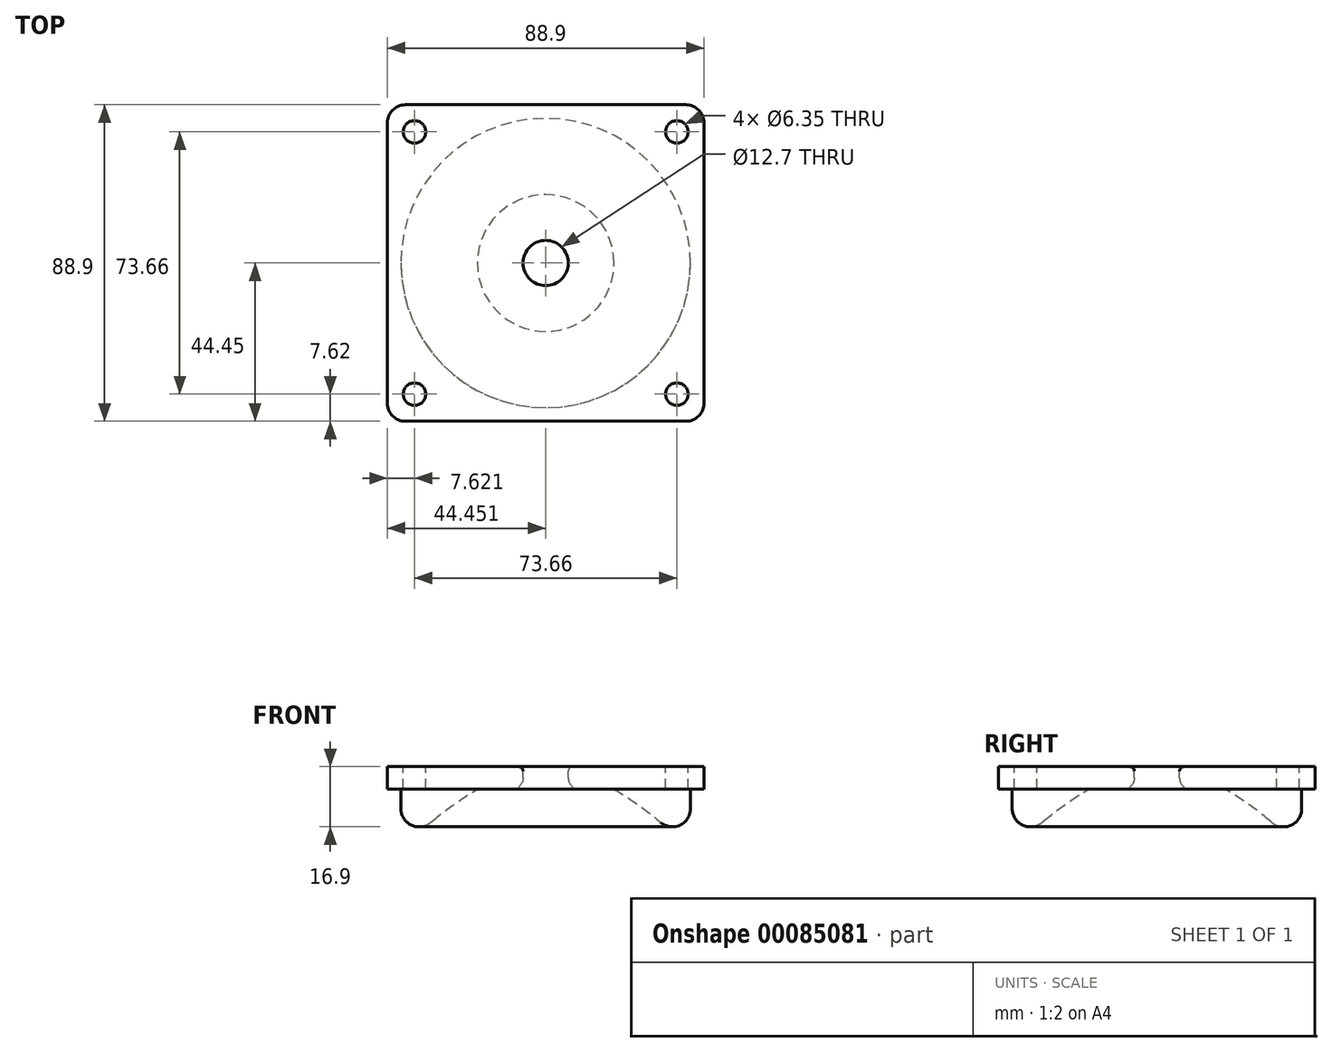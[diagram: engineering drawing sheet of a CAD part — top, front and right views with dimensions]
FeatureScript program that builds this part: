
annotation { "Feature Type Name" : "Feature", "Feature Type Description" : "" }
export const myFeature = defineFeature(function(context is Context, id is Id, definition is map)
    precondition{}
    {
        {
            var Q0;
            Q0=qCreatedBy(makeId("Front.planeOp"),FACE);
            var sketch = newSketch(context, id + "F0", { "sketchPlane" : qUnion([Q0])});
            skLineSegment(sketch, "E0", {"start": v(4.17, 45.04) * mm, "end": v(4.17, -20.37) * mm});
            skLineSegment(sketch, "E1", {"start": v(10.52, 12.1) * mm, "end": v(10.52, 30.43) * mm});
            skLineSegment(sketch, "E2.bottom", {"start": v(10.52, 30.43) * mm, "end": v(61.32, 30.43) * mm});
            skLineSegment(sketch, "E2.top", {"start": v(10.52, 24.08) * mm, "end": v(61.32, 24.08) * mm});
            skLineSegment(sketch, "E2.left", {"start": v(10.52, 30.43) * mm, "end": v(10.52, 24.08) * mm});
            skLineSegment(sketch, "E2.right", {"start": v(61.32, 30.43) * mm, "end": v(61.32, 24.08) * mm});
            skLineSegment(sketch, "E3", {"start": v(35.92, 15.19) * mm, "end": v(35.92, 24.08) * mm});
            skCircle(sketch, "E4", {"center": v(4.17, -20.37) * mm, "radius": 31.75 * mm});
            skFitSpline(sketch, "E5", {"points": [v(10.52, 30.43) * mm, v(35.92, 15.19) * mm, v(55.36, -11.12) * mm, v(53.77, -25.69) * mm, v(41.93, -25.69) * mm, v(36.47, -11.57) * mm, v(24.29, 4.78) * mm, v(10.52, 12.1) * mm], "startDerivative": vector(142.65, -59.66) * mm, "endDerivative": vector(-100.84, 59.34) * mm});
            skLineSegment(sketch, "E6", {"start": v(44.81, 24.08) * mm, "end": v(44.81, 6.32) * mm});
            skSolve(sketch);
        }
        {
            var Q0;
            {var subQ5=sQuery(id+"F0.wireOp",EDGE,"E2.bottom");Q0=makeQuery(id+"F0.imprint","IMPRINT",FACE,{"disambiguationData":[TD([[makeQuery(id+"F0.imprint","IMPRINT",EDGE,{"derivedFrom":subQ5}),-1.0]])]});}
            var Q1;
            {var subQ0=sQuery(id+"F0.wireOp",EDGE,"E2.left");Q1=makeQuery(id+"F0.imprint","IMPRINT",FACE,{"disambiguationData":[TD([[makeQuery(id+"F0.imprint","IMPRINT",EDGE,{"derivedFrom":subQ0}),1.0]])]});}
            var Q2;
            {var subQ0=sQuery(id+"F0.wireOp",EDGE,"E3");Q2=makeQuery(id+"F0.imprint","IMPRINT",FACE,{"disambiguationData":[TD([[makeQuery(id+"F0.imprint","IMPRINT",EDGE,{"derivedFrom":subQ0}),1.0]])]});}
            var Q3;
            {var subQ0=sQuery(id+"F0.wireOp",EDGE,"E1");Q3=makeQuery(id+"F0.imprint","IMPRINT",FACE,{"disambiguationData":[TD([[makeQuery(id+"F0.imprint","IMPRINT",EDGE,{"derivedFrom":subQ0}),-1.0]])]});}
            var Q4;
            {var subQ0=sQuery(id+"F0.wireOp",EDGE,"E3");Q4=makeQuery(id+"F0.imprint","IMPRINT",FACE,{"disambiguationData":[TD([[makeQuery(id+"F0.imprint","IMPRINT",EDGE,{"derivedFrom":subQ0}),-1.0]])]});}
            var Q5;
            Q5=sQuery(id+"F0.wireOp",EDGE,"E0");
            revolve(context, id + "F1", {"entities" : qUnion([Q0, Q1, Q2, Q3, Q4]), "axis" : qUnion([Q5]), "revolveType" : RevolveType.FULL});
        }
        {
            var Q0;
            Q0=makeQuery(id+"F1.opRevolve","SWEPT_EDGE",EDGE,{"disambiguationData":[OSD([sQuery(id+"F0.wireOp",EDGE,"E5"),sQuery(id+"F0.wireOp",EDGE,"E6")])]});
            fillet(context, id + "F2", {"entities" : qUnion([Q0]), "radius" : 5.08 * mm, "tangentPropagation" : true, "allowEdgeOverflow" : false});
        }
        {
            var Q0;
            Q0=makeQuery(id+"F1.opRevolve","SWEPT_FACE",FACE,{"disambiguationData":[OSD([sQuery(id+"F0.wireOp",EDGE,"E2.bottom")])]});
            var sketch = newSketch(context, id + "F3", { "sketchPlane" : qUnion([Q0])});
            skLineSegment(sketch, "E7.bottom", {"start": v(-52.98, 57.15) * mm, "end": v(61.32, 57.15) * mm});
            skLineSegment(sketch, "E7.top", {"start": v(-52.98, -57.15) * mm, "end": v(61.32, -57.15) * mm});
            skLineSegment(sketch, "E7.left", {"start": v(-52.98, 57.15) * mm, "end": v(-52.98, -57.15) * mm});
            skLineSegment(sketch, "E7.right", {"start": v(61.32, 57.15) * mm, "end": v(61.32, -57.15) * mm});
            skCircle(sketch, "E8", {"center": v(-32.66, 36.83) * mm, "radius": 3.18 * mm});
            skCircle(sketch, "E9", {"center": v(41, 36.83) * mm, "radius": 3.18 * mm});
            skCircle(sketch, "E10", {"center": v(41, -36.83) * mm, "radius": 3.18 * mm});
            skCircle(sketch, "E11", {"center": v(-32.66, -36.83) * mm, "radius": 3.18 * mm});
            skLineSegment(sketch, "E12.bottom", {"start": v(-40.28, 44.45) * mm, "end": v(48.62, 44.45) * mm});
            skLineSegment(sketch, "E12.top", {"start": v(-40.28, -44.45) * mm, "end": v(48.62, -44.45) * mm});
            skLineSegment(sketch, "E12.left", {"start": v(-40.28, 44.45) * mm, "end": v(-40.28, -44.45) * mm});
            skLineSegment(sketch, "E12.right", {"start": v(48.62, 44.45) * mm, "end": v(48.62, -44.45) * mm});
            skSolve(sketch);
        }
        {
            var Q0;
            Q0=makeQuery(id+"F3.imprint","IMPRINT",FACE,{"disambiguationData":[TD([[makeQuery(id+"F3.imprint","IMPRINT",EDGE,{"derivedFrom":sQuery(id+"F3.wireOp",EDGE,"E9")}),1.0]])]});
            var Q1;
            Q1=makeQuery(id+"F3.imprint","IMPRINT",FACE,{"disambiguationData":[TD([[makeQuery(id+"F3.imprint","IMPRINT",EDGE,{"derivedFrom":sQuery(id+"F3.wireOp",EDGE,"E10")}),1.0]])]});
            var Q2;
            Q2=makeQuery(id+"F3.imprint","IMPRINT",FACE,{"disambiguationData":[TD([[makeQuery(id+"F3.imprint","IMPRINT",EDGE,{"derivedFrom":sQuery(id+"F3.wireOp",EDGE,"E11")}),1.0]])]});
            var Q3;
            Q3=makeQuery(id+"F3.imprint","IMPRINT",FACE,{"disambiguationData":[TD([[makeQuery(id+"F3.imprint","IMPRINT",EDGE,{"derivedFrom":sQuery(id+"F3.wireOp",EDGE,"E8")}),1.0]])]});
            var Q4;
            {var subQ0=sQuery(id+"F3.wireOp",EDGE,"E12.bottom");var subQ1=makeQuery(id+"F1.opRevolve","SWEPT_EDGE",EDGE,{"disambiguationData":[OSD([sQuery(id+"F0.wireOp",EDGE,"E2.bottom"),sQuery(id+"F0.wireOp",EDGE,"E2.right")])]});var subQ2=makeQuery(id+"F3.imprint","INTERSECT",VERTEX,{"disambiguationData":[OD(0.0)],"derivedFrom":[subQ1,subQ0]});Q4=makeQuery(id+"F3.imprint","IMPRINT",FACE,{"disambiguationData":[TD([[makeQuery(id+"F3.imprint","IMPRINT",EDGE,{"disambiguationData":[TD([[subQ2,-1.0]])],"derivedFrom":subQ0}),1.0]])]});}
            var Q5;
            {var subQ0=sQuery(id+"F3.wireOp",EDGE,"E12.left");var subQ1=makeQuery(id+"F1.opRevolve","SWEPT_EDGE",EDGE,{"disambiguationData":[OSD([sQuery(id+"F0.wireOp",EDGE,"E2.bottom"),sQuery(id+"F0.wireOp",EDGE,"E2.right")])]});var subQ2=makeQuery(id+"F3.imprint","INTERSECT",VERTEX,{"disambiguationData":[OD(0.0)],"derivedFrom":[subQ1,subQ0]});Q5=makeQuery(id+"F3.imprint","IMPRINT",FACE,{"disambiguationData":[TD([[makeQuery(id+"F3.imprint","IMPRINT",EDGE,{"disambiguationData":[TD([[subQ2,-1.0]])],"derivedFrom":subQ0}),-1.0]])]});}
            var Q6;
            {var subQ0=sQuery(id+"F3.wireOp",EDGE,"E12.right");var subQ1=makeQuery(id+"F1.opRevolve","SWEPT_EDGE",EDGE,{"disambiguationData":[OSD([sQuery(id+"F0.wireOp",EDGE,"E2.bottom"),sQuery(id+"F0.wireOp",EDGE,"E2.right")])]});var subQ2=makeQuery(id+"F3.imprint","INTERSECT",VERTEX,{"disambiguationData":[OD(0.0)],"derivedFrom":[subQ1,subQ0]});Q6=makeQuery(id+"F3.imprint","IMPRINT",FACE,{"disambiguationData":[TD([[makeQuery(id+"F3.imprint","IMPRINT",EDGE,{"disambiguationData":[TD([[subQ2,-1.0]])],"derivedFrom":subQ0}),1.0]])]});}
            var Q7;
            {var subQ0=sQuery(id+"F3.wireOp",EDGE,"E12.top");var subQ1=makeQuery(id+"F1.opRevolve","SWEPT_EDGE",EDGE,{"disambiguationData":[OSD([sQuery(id+"F0.wireOp",EDGE,"E2.bottom"),sQuery(id+"F0.wireOp",EDGE,"E2.right")])]});var subQ2=makeQuery(id+"F3.imprint","INTERSECT",VERTEX,{"disambiguationData":[OD(0.0)],"derivedFrom":[subQ1,subQ0]});Q7=makeQuery(id+"F3.imprint","IMPRINT",FACE,{"disambiguationData":[TD([[makeQuery(id+"F3.imprint","IMPRINT",EDGE,{"disambiguationData":[TD([[subQ2,-1.0]])],"derivedFrom":subQ0}),-1.0]])]});}
            var Q8;
            {var subQ0=sQuery(id+"F3.wireOp",EDGE,"E12.right");var subQ1=sQuery(id+"F3.wireOp",EDGE,"E12.top");var subQ2=makeQuery(id+"F3.imprint","INTERSECT",VERTEX,{"derivedFrom":[subQ1,subQ0]});Q8=makeQuery(id+"F3.imprint","IMPRINT",FACE,{"disambiguationData":[TD([[makeQuery(id+"F3.imprint","IMPRINT",EDGE,{"disambiguationData":[TD([[subQ2,1.0]])],"derivedFrom":subQ1}),1.0]])]});}
            var Q9;
            {var subQ0=sQuery(id+"F3.wireOp",EDGE,"E12.left");var subQ1=sQuery(id+"F3.wireOp",EDGE,"E12.top");var subQ2=makeQuery(id+"F3.imprint","INTERSECT",VERTEX,{"derivedFrom":[subQ1,subQ0]});Q9=makeQuery(id+"F3.imprint","IMPRINT",FACE,{"disambiguationData":[TD([[makeQuery(id+"F3.imprint","IMPRINT",EDGE,{"disambiguationData":[TD([[subQ2,-1.0]])],"derivedFrom":subQ1}),1.0]])]});}
            var Q10;
            {var subQ0=sQuery(id+"F3.wireOp",EDGE,"E12.right");var subQ1=sQuery(id+"F3.wireOp",EDGE,"E12.bottom");var subQ2=makeQuery(id+"F3.imprint","INTERSECT",VERTEX,{"derivedFrom":[subQ1,subQ0]});Q10=makeQuery(id+"F3.imprint","IMPRINT",FACE,{"disambiguationData":[TD([[makeQuery(id+"F3.imprint","IMPRINT",EDGE,{"disambiguationData":[TD([[subQ2,1.0]])],"derivedFrom":subQ1}),-1.0]])]});}
            var Q11;
            Q11=makeQuery(id+"F1.opRevolve","SWEPT_FACE",FACE,{"disambiguationData":[OSD([sQuery(id+"F0.wireOp",EDGE,"E2.top")])]});
            extrude(context, id + "F4", {"entities" : qUnion([Q0, Q1, Q2, Q3, Q4, Q5, Q6, Q7, Q8, Q9, Q10]), "operationType" : NewBodyOperationType.REMOVE, "endBound" : BoundingType.UP_TO_SURFACE, "oppositeDirection" : true, "endBoundEntityFace" : qUnion([Q11]), "depth" : 25.4 * mm});
        }
        {
            var Q0;
            Q0=makeQuery(id+"F1.opRevolve","SWEPT_EDGE",EDGE,{"disambiguationData":[OSD([sQuery(id+"F0.wireOp",EDGE,"26433d5a-ca9f-40aa-9ac8-344165d94d51"),sQuery(id+"F0.wireOp",EDGE,"E1")])]});
            fillet(context, id + "F5", {"entities" : qUnion([Q0]), "radius" : 3.17 * mm, "tangentPropagation" : true, "allowEdgeOverflow" : false});
        }
        {
            var Q0;
            {var subQ0=sQuery(id+"F3.wireOp",EDGE,"E12.left");var subQ1=sQuery(id+"F3.wireOp",EDGE,"E12.bottom");var subQ2=makeQuery(id+"F3.imprint","INTERSECT",VERTEX,{"derivedFrom":[subQ1,subQ0]});Q0=makeQuery(id+"F3.imprint","IMPRINT",FACE,{"disambiguationData":[TD([[makeQuery(id+"F3.imprint","IMPRINT",EDGE,{"disambiguationData":[TD([[subQ2,-1.0]])],"derivedFrom":subQ1}),-1.0]])]});}
            var Q1;
            {var subQ0=sQuery(id+"F3.wireOp",EDGE,"E12.left");var subQ1=sQuery(id+"F3.wireOp",EDGE,"E12.top");var subQ2=makeQuery(id+"F3.imprint","INTERSECT",VERTEX,{"derivedFrom":[subQ1,subQ0]});Q1=makeQuery(id+"F3.imprint","IMPRINT",FACE,{"disambiguationData":[TD([[makeQuery(id+"F3.imprint","IMPRINT",EDGE,{"disambiguationData":[TD([[subQ2,-1.0]])],"derivedFrom":subQ1}),1.0]])]});}
            var Q2;
            {var subQ0=sQuery(id+"F3.wireOp",EDGE,"E12.right");var subQ1=sQuery(id+"F3.wireOp",EDGE,"E12.top");var subQ2=makeQuery(id+"F3.imprint","INTERSECT",VERTEX,{"derivedFrom":[subQ1,subQ0]});Q2=makeQuery(id+"F3.imprint","IMPRINT",FACE,{"disambiguationData":[TD([[makeQuery(id+"F3.imprint","IMPRINT",EDGE,{"disambiguationData":[TD([[subQ2,1.0]])],"derivedFrom":subQ1}),1.0]])]});}
            var Q3;
            {var subQ0=sQuery(id+"F3.wireOp",EDGE,"E12.right");var subQ1=sQuery(id+"F3.wireOp",EDGE,"E12.bottom");var subQ2=makeQuery(id+"F3.imprint","INTERSECT",VERTEX,{"derivedFrom":[subQ1,subQ0]});Q3=makeQuery(id+"F3.imprint","IMPRINT",FACE,{"disambiguationData":[TD([[makeQuery(id+"F3.imprint","IMPRINT",EDGE,{"disambiguationData":[TD([[subQ2,1.0]])],"derivedFrom":subQ1}),-1.0]])]});}
            var Q4;
            Q4=makeQuery(id+"F1.opRevolve","SWEPT_FACE",FACE,{"disambiguationData":[OSD([sQuery(id+"F0.wireOp",EDGE,"E2.top")])]});
            extrude(context, id + "F6", {"entities" : qUnion([Q0, Q1, Q2, Q3]), "operationType" : NewBodyOperationType.ADD, "endBound" : BoundingType.UP_TO_SURFACE, "oppositeDirection" : true, "endBoundEntityFace" : qUnion([Q4]), "depth" : 25.4 * mm});
        }
        {
            var Q0;
            Q0=makeQuery(id+"F6.opExtrude","SWEPT_EDGE",EDGE,{"disambiguationData":[OSD([sQuery(id+"F3.wireOp",EDGE,"E12.bottom"),sQuery(id+"F3.wireOp",EDGE,"E12.left")])]});
            var Q1;
            Q1=makeQuery(id+"F6.opExtrude","SWEPT_EDGE",EDGE,{"disambiguationData":[OSD([sQuery(id+"F3.wireOp",EDGE,"E12.bottom"),sQuery(id+"F3.wireOp",EDGE,"E12.right")])]});
            var Q2;
            Q2=makeQuery(id+"F6.opExtrude","SWEPT_EDGE",EDGE,{"disambiguationData":[OSD([sQuery(id+"F3.wireOp",EDGE,"E12.top"),sQuery(id+"F3.wireOp",EDGE,"E12.right")])]});
            var Q3;
            Q3=makeQuery(id+"F6.opExtrude","SWEPT_EDGE",EDGE,{"disambiguationData":[OSD([sQuery(id+"F3.wireOp",EDGE,"E12.top"),sQuery(id+"F3.wireOp",EDGE,"E12.left")])]});
            fillet(context, id + "F7", {"entities" : qUnion([Q0, Q1, Q2, Q3]), "radius" : 5.08 * mm, "tangentPropagation" : true, "allowEdgeOverflow" : false});
        }
        {
            var Q0;
            Q0=makeQuery(id+"F1.opRevolve","SWEPT_EDGE",EDGE,{"disambiguationData":[OSD([sQuery(id+"F0.wireOp",EDGE,"E2.bottom"),sQuery(id+"F0.wireOp",EDGE,"E2.left"),sQuery(id+"F0.wireOp",EDGE,"E5")])]});
            fillet(context, id + "F8", {"entities" : qUnion([Q0]), "radius" : 1.27 * mm, "tangentPropagation" : true, "allowEdgeOverflow" : false});
        }
    });
